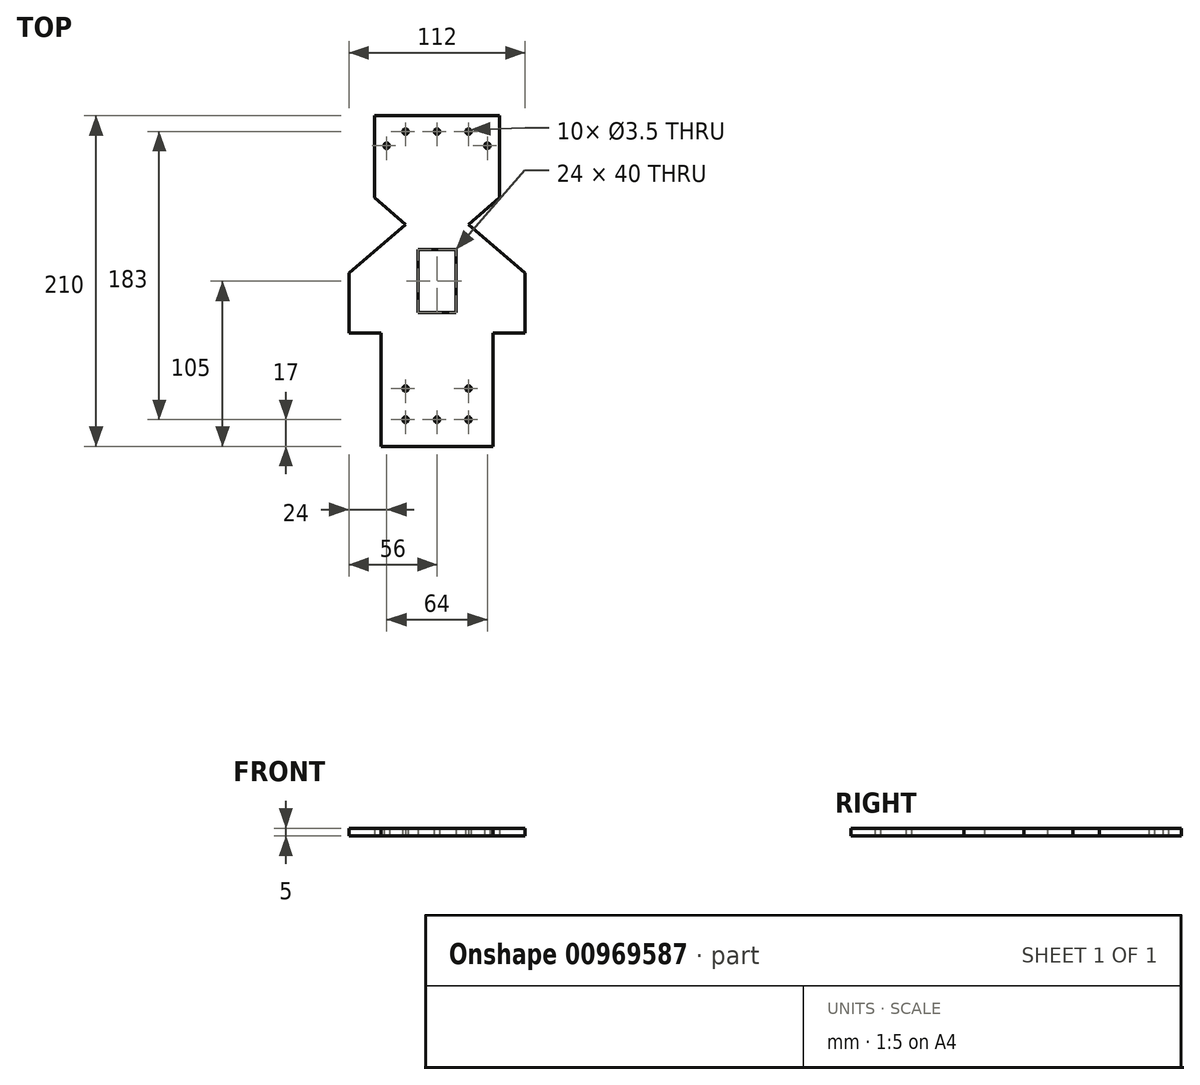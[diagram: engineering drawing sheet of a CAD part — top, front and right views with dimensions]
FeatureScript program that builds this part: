
annotation { "Feature Type Name" : "Feature", "Feature Type Description" : "" }
export const myFeature = defineFeature(function(context is Context, id is Id, definition is map)
    precondition{}
    {
        {
            var Q0;
            Q0=qCreatedBy(makeId("Top.planeOp"),FACE);
            var sketch = newSketch(context, id + "F0", { "sketchPlane" : qUnion([Q0])});
            skCircle(sketch, "E0", {"center": v(-20, -88) * mm, "radius": 1.75 * mm});
            skCircle(sketch, "E1", {"center": v(0, -88) * mm, "radius": 1.75 * mm});
            skCircle(sketch, "E2", {"center": v(20, -88) * mm, "radius": 1.75 * mm});
            skCircle(sketch, "E3", {"center": v(-20, -68.25) * mm, "radius": 1.75 * mm});
            skCircle(sketch, "E4", {"center": v(20, -68.25) * mm, "radius": 1.75 * mm});
            skCircle(sketch, "E5", {"center": v(-20, 95) * mm, "radius": 1.75 * mm});
            skCircle(sketch, "E6", {"center": v(0, 95) * mm, "radius": 1.75 * mm});
            skCircle(sketch, "E7", {"center": v(20, 95) * mm, "radius": 1.75 * mm});
            skCircle(sketch, "E8", {"center": v(-32, 86) * mm, "radius": 1.75 * mm});
            skCircle(sketch, "E9", {"center": v(32, 86) * mm, "radius": 1.75 * mm});
            skLineSegment(sketch, "E10.bottom", {"start": v(56, -105) * mm, "end": v(-56, -105) * mm});
            skLineSegment(sketch, "E10.top", {"start": v(56, 105) * mm, "end": v(-56, 105) * mm});
            skLineSegment(sketch, "E10.left", {"start": v(56, -105) * mm, "end": v(56, 105) * mm});
            skLineSegment(sketch, "E10.right", {"start": v(-56, -105) * mm, "end": v(-56, 105) * mm});
            skLineSegment(sketch, "E11", {"start": v(-56, 67) * mm, "end": v(-20, 36.01) * mm});
            skLineSegment(sketch, "E12", {"start": v(-20, 36.01) * mm, "end": v(-56, 5.02) * mm});
            skLineSegment(sketch, "E13.MirrorCS", {"start": v(56, 67) * mm, "end": v(20, 36.01) * mm});
            skLineSegment(sketch, "E14.MirrorCS", {"start": v(20, 36.01) * mm, "end": v(56, 5.02) * mm});
            skLineSegment(sketch, "E15", {"start": v(-56, -33) * mm, "end": v(-35.5, -33) * mm});
            skLineSegment(sketch, "E16", {"start": v(-35.5, -33) * mm, "end": v(-35.5, -105) * mm});
            skLineSegment(sketch, "E17.MirrorCS", {"start": v(56, -33) * mm, "end": v(35.5, -33) * mm});
            skLineSegment(sketch, "E18.MirrorCS", {"start": v(35.5, -33) * mm, "end": v(35.5, -105) * mm});
            skLineSegment(sketch, "E19", {"start": v(39.74, 105) * mm, "end": v(39.74, 53) * mm});
            skLineSegment(sketch, "E20.MirrorCS", {"start": v(-39.74, 105) * mm, "end": v(-39.74, 53) * mm});
            skLineSegment(sketch, "E21.bottom", {"start": v(-12, 20) * mm, "end": v(12, 20) * mm});
            skLineSegment(sketch, "E21.top", {"start": v(-12, -20) * mm, "end": v(12, -20) * mm});
            skLineSegment(sketch, "E21.left", {"start": v(-12, 20) * mm, "end": v(-12, -20) * mm});
            skLineSegment(sketch, "E21.right", {"start": v(12, 20) * mm, "end": v(12, -20) * mm});
            skSolve(sketch);
        }
        {
            var Q0;
            Q0=makeQuery(id+"F0.imprint","IMPRINT",FACE,{"disambiguationData":[TD([[makeQuery(id+"F0.imprint","IMPRINT",EDGE,{"derivedFrom":sQuery(id+"F0.wireOp",EDGE,"E0")}),-1.0]])]});
            extrude(context, id + "F1", {"entities" : qUnion([Q0]), "depth" : 5 * mm, "offsetDistance" : 25 * mm});
        }
    });
